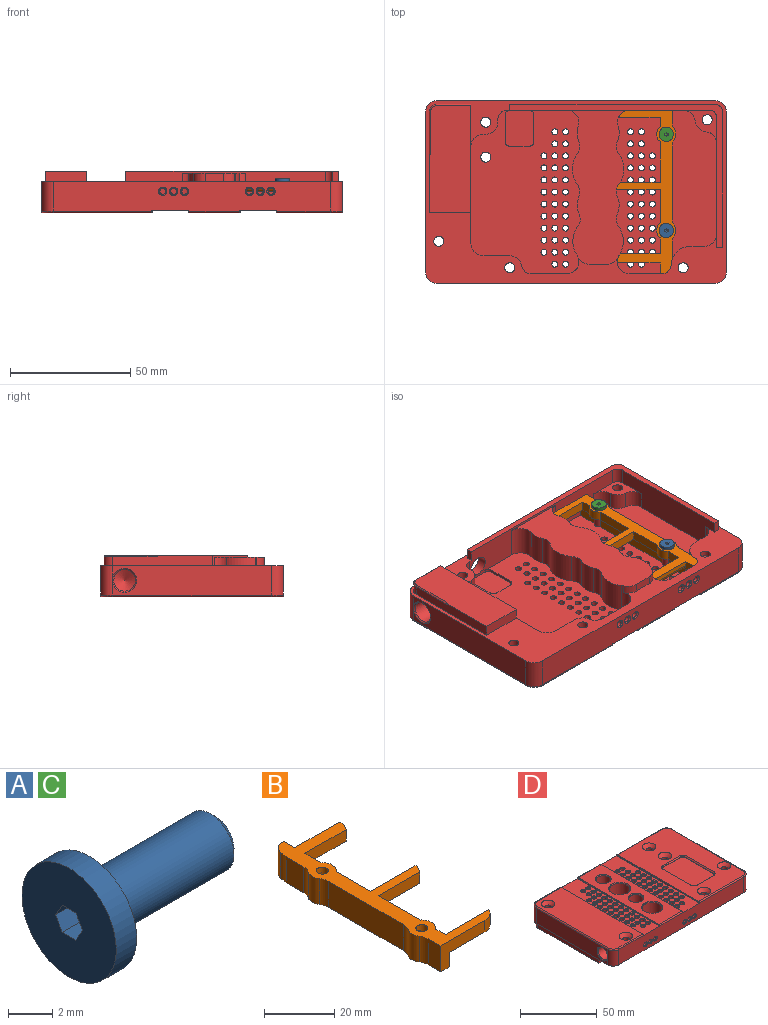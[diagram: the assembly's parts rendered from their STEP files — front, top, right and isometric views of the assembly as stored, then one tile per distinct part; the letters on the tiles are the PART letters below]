
ASSEMBLY  parts=4 mates=3
PART A: 20 faces, bbox 9.3x6x6 mm
  f0: cylinder r=3mm len=6mm, axis (-1,0,0), area 24.5mm2, adj f1,f13
  f1: plane 6x6mm, normal (-1,0,0), area 26.3mm2, adj f0,f2,f3,f4,f5,f6,f7
  f2: plane 2x0.75mm, normal (0,-0.87,0.5), area 1.7mm2, adj f1,f3,f4,f16,f17
  f3: plane 2x0.75mm, normal (0,-0.87,-0.5), area 1.7mm2, adj f1,f2,f7,f17,f18
  f4: plane 2x0.87mm, normal (0,0,1), area 1.7mm2, adj f1,f2,f5,f14,f16
  f5: plane 2x0.75mm, normal (0,0.87,0.5), area 1.7mm2, adj f1,f4,f6,f14,f15
  f6: plane 2x0.75mm, normal (0,0.87,-0.5), area 1.7mm2, adj f1,f5,f7,f15,f19
  f7: plane 2x0.87mm, normal (0,0,-1), area 1.7mm2, adj f1,f3,f6,f18,f19
  f8: cone r=0.75mm half-angle=60deg, axis (-1,0,0), area 2mm2, adj f14,f15,f16,f17,f18,f19
  f9: plane 2.39x2.39mm, normal (1,0,0), area 4.5mm2, adj f10
  f10: cone r=1.5mm half-angle=45deg, axis (-1,0,0), area 3.7mm2, adj f9,f11
  f11: cylinder r=1.5mm len=7.59mm, axis (-1,0,0), area 71.6mm2, adj f10,f12
  f12: torus R=1.6mm, axis (1,0,0), area 1.5mm2, adj f11,f13
  f13: plane 6x6mm, normal (1,0,0), area 20.2mm2, adj f0,f12
  f14: plane 0.65x0.38mm, normal (-1,0,0), area 0mm2, adj f4,f5,f8
  f15: plane 0.75x0.22mm, normal (-1,0,0), area 0mm2, adj f5,f6,f8
  f16: plane 0.65x0.38mm, normal (-1,0,0), area 0mm2, adj f2,f4,f8
  f17: plane 0.75x0.22mm, normal (-1,0,0), area 0mm2, adj f2,f3,f8
  f18: plane 0.65x0.38mm, normal (-1,0,0), area 0mm2, adj f3,f7,f8
  f19: plane 0.65x0.38mm, normal (-1,0,0), area 0mm2, adj f6,f7,f8
PART B: 47 faces, bbox 24.7x68x9 mm
  f0: plane 16.57x4mm, normal (0,-1,0), area 66.3mm2, adj f1,f21,f32,f46
  f1: plane 68x19.65mm, normal (0,0,-1), area 247.5mm2, adj f0,f3,f4,f5,f6,f9,f10,f11
  f2: plane 17.81x2mm, normal (0,1,0), area 35.6mm2, adj f3,f4,f32,f45
  f3: cylinder r=2mm len=17.84mm, axis (-1,0,0), area 55.9mm2, adj f1,f2,f4,f45
  f4: plane 6.5x4mm, normal (1,0,0), area 18.9mm2, adj f1,f2,f3,f22,f32
  f5: plane 36.42x5mm, normal (1,0,0), area 182.1mm2, adj f1,f33,f34,f36
  f6: plane 16.11x5mm, normal (1,0,0), area 80.6mm2, adj f1,f23,f33,f36
  f7: plane 4.1x3.05mm, normal (0,0,-1), area 2.8mm2, adj f29,f33,f37,f40
  f8: plane 4.1x3.05mm, normal (0,0,-1), area 2.8mm2, adj f31,f34,f38,f39
  f9: plane 17.81x9mm, normal (0,-1,0), area 88.7mm2, adj f1,f10,f30,f32,f35,f36
  f10: cylinder r=5mm len=4.58mm, axis (0,0,-1), area 23.2mm2, adj f1,f9,f11,f32
  f11: plane 17.39x4mm, normal (0,1,0), area 69.6mm2, adj f1,f10,f12,f32
  f12: plane 4x3.88mm, normal (1,0,0), area 15.5mm2, adj f1,f11,f13,f32
  f13: cylinder r=4mm len=6.25mm, axis (0,0,-1), area 28.7mm2, adj f1,f12,f14,f32
  f14: plane 16.88x4mm, normal (1,0,0), area 67.5mm2, adj f1,f13,f15,f32
  f15: plane 16.62x4mm, normal (0,-1,0), area 66.5mm2, adj f1,f14,f16,f32
  f16: cylinder r=10.7mm len=4mm, axis (0,0,-1), area 4.4mm2, adj f1,f15,f17,f32
  f17: cylinder r=5mm len=4mm, axis (0,0,-1), area 9.2mm2, adj f1,f16,f18,f32
  f18: plane 18.15x4mm, normal (0,1,0), area 72.6mm2, adj f1,f17,f19,f32
  f19: plane 13.88x4mm, normal (1,0,0), area 55.5mm2, adj f1,f18,f20,f32
  f20: cylinder r=4mm len=6.25mm, axis (0,0,-1), area 28.7mm2, adj f1,f19,f21,f32
  f21: plane 6.38x4mm, normal (1,0,0), area 25.5mm2, adj f0,f1,f20,f32
  f22: plane 4x0.63mm, normal (0,1,0), area 2.5mm2, adj f1,f4,f23,f32
  f23: cylinder r=4mm len=9mm, axis (0,0,-1), area 46.1mm2, adj f1,f6,f22,f24,f32,f36
  f24: cylinder r=8.17mm len=9mm, axis (0,0,-1), area 24mm2, adj f23,f25,f32,f36
  f25: plane 9x7.08mm, normal (-1,0,0), area 63.7mm2, adj f24,f32,f36,f42
  f26: cylinder r=4mm len=9mm, axis (0,0,-1), area 42.2mm2, adj f32,f36,f41,f42
  f27: plane 30.05x9mm, normal (-1,0,0), area 270.5mm2, adj f32,f36,f41,f43
  f28: cylinder r=4mm len=9mm, axis (0,0,-1), area 42.2mm2, adj f32,f36,f43,f44
  f29: cylinder r=1.7mm len=4mm, axis (0,0,-1), area 27.8mm2, adj f1,f7,f32,f37,f40
  f30: plane 9x5.03mm, normal (-1,0,0), area 45.2mm2, adj f9,f32,f36,f44
  f31: cylinder r=1.7mm len=4mm, axis (0,0,-1), area 27.8mm2, adj f1,f8,f32,f38,f39
  f32: plane 68x24.65mm, normal (0,0,1), area 514.5mm2, adj f0,f2,f4,f9,f10,f11,f12,f13
  f33: cylinder r=2.05mm len=7mm, axis (0,0,1), area 59.7mm2, adj f5,f6,f7,f36,f37,f40
  f34: cylinder r=2.05mm len=7mm, axis (0,0,1), area 59.7mm2, adj f5,f8,f35,f36,f38,f39
  f35: plane 8.21x5mm, normal (1,0,0), area 41.1mm2, adj f1,f9,f34,f36
  f36: plane 67.9x5mm, normal (0,0,-1), area 225.9mm2, adj f5,f6,f9,f23,f24,f25,f26,f27
  f37: plane 2x0.41mm, normal (-1,0,0), area 0.8mm2, adj f1,f7,f29,f33
  f38: plane 2x0.41mm, normal (-1,0,0), area 0.8mm2, adj f1,f8,f31,f34
  f39: plane 2x0.41mm, normal (-1,0,0), area 0.8mm2, adj f1,f8,f31,f34
  f40: plane 2x0.41mm, normal (-1,0,0), area 0.8mm2, adj f1,f7,f29,f33
  f41: cylinder r=5mm len=9mm, axis (0,0,-1), area 26.4mm2, adj f26,f27,f32,f36
  f42: cylinder r=5mm len=9mm, axis (0,0,-1), area 26.4mm2, adj f25,f26,f32,f36
  f43: cylinder r=5mm len=9mm, axis (0,0,-1), area 26.4mm2, adj f27,f28,f32,f36
  f44: cylinder r=5mm len=9mm, axis (0,0,-1), area 26.4mm2, adj f28,f30,f32,f36
  f45: cylinder r=5mm len=4mm, axis (0,0,1), area 12.8mm2, adj f1,f2,f3,f32,f46
  f46: cylinder r=10.5mm len=4mm, axis (0,0,1), area 3.5mm2, adj f0,f1,f32,f45
PART C: same geometry as A
PART D: 320 faces, bbox 126.1x77.1x17.7 mm
  f0: plane 68x45.38mm, normal (0,0,-1), area 2357.2mm2, adj f2,f4,f5,f6,f10,f12,f27,f53
  f1: plane 64x25.99mm, normal (0,0,-1), area 1135mm2, adj f2,f3,f4,f5,f6,f7,f8,f9
  f2: cylinder r=5mm len=12.4mm, axis (0,0,1), area 95.7mm2, adj f0,f1,f6,f10,f13,f221,f300
  f3: cylinder r=5mm len=12.4mm, axis (0,0,1), area 99.7mm2, adj f1,f11,f13,f25,f29,f301
  f4: cylinder r=10.7mm len=12.83mm, axis (0,0,1), area 170.6mm2, adj f0,f1,f219,f220
  f5: cylinder r=8.75mm len=12.4mm, axis (0,0,1), area 92.6mm2, adj f0,f1,f218,f219
  f6: cylinder r=10.5mm len=12.4mm, axis (0,0,1), area 158.4mm2, adj f0,f1,f2,f218
  f7: cylinder r=8.75mm len=12.4mm, axis (0,0,1), area 81.6mm2, adj f1,f29,f214,f217
  f8: cylinder r=10.7mm len=12.83mm, axis (0,0,1), area 170.6mm2, adj f1,f29,f216,f217
  f9: cylinder r=8.75mm len=12.4mm, axis (0,0,1), area 92.6mm2, adj f1,f29,f215,f216
  f10: plane 14.86x9mm, normal (0,1,0), area 123mm2, adj f0,f2,f13,f134,f221,f225,f226
  f11: cylinder r=10.5mm len=12.4mm, axis (0,0,1), area 158.4mm2, adj f1,f3,f29,f215
  f12: cylinder r=8.75mm len=12.4mm, axis (0,0,1), area 81.6mm2, adj f0,f1,f213,f220
  f13: plane 125x76mm, normal (0,0,-1), area 1906.4mm2, adj f2,f3,f10,f14,f17,f18,f25,f26
  f14: cylinder r=2.1mm len=10.7mm, axis (0,0,1), area 111mm2, adj f13,f56,f184,f185
  f15: cylinder r=5mm len=7mm, axis (0,0,1), area 51.5mm2, adj f27,f29,f52,f163
  f16: cylinder r=5mm len=7mm, axis (0,0,1), area 51.5mm2, adj f26,f29,f52,f163
  f17: plane 115x12.2mm, normal (0,-1,0), area 1339.1mm2, adj f13,f21,f22,f30,f31,f39,f137,f140
  f18: plane 115x12.2mm, normal (0,1,0), area 1344mm2, adj f13,f23,f24,f33,f34,f42,f137,f140
  f19: plane 74.4x21.1mm, normal (0,0,1), area 1094.6mm2, adj f21,f23,f150,f160,f209,f210,f211,f212
  f20: plane 74.4x26.55mm, normal (0,0,1), area 1846.1mm2, adj f22,f24,f41,f43,f44,f56,f59,f145
  f21: cylinder r=0.8mm len=21.1mm, axis (-1,0,0), area 26.5mm2, adj f17,f19,f151,f161
  f22: cylinder r=0.8mm len=22.35mm, axis (-1,0,0), area 28.1mm2, adj f17,f20,f41,f146
  f23: cylinder r=0.8mm len=21.1mm, axis (1,0,0), area 26.5mm2, adj f18,f19,f149,f159
  f24: cylinder r=0.8mm len=22.35mm, axis (1,0,0), area 28.1mm2, adj f18,f20,f44,f144
  f25: plane 13.46x9mm, normal (0,1,0), area 106.5mm2, adj f3,f13,f29,f135,f222,f223,f224
  f26: plane 54x13.42mm, normal (1,0,0), area 598.3mm2, adj f13,f16,f29,f128,f130,f163,f183,f199
  f27: plane 84x14.42mm, normal (0,-1,0), area 678.8mm2, adj f0,f1,f13,f15,f29,f128,f129,f136
  f28: plane 56x4.42mm, normal (-1,0,0), area 247.2mm2, adj f13,f60,f130,f199
  f29: plane 68x41.83mm, normal (0,0,-1), area 2259.8mm2, adj f3,f7,f8,f9,f11,f15,f16,f25
  f30: cylinder r=5mm len=12.2mm, axis (0,0,-1), area 95.8mm2, adj f13,f17,f35,f41
  f31: cylinder r=5mm len=12.2mm, axis (0,0,-1), area 95.8mm2, adj f13,f17,f32,f37
  f32: plane 66x12.2mm, normal (1,0,0), area 726.7mm2, adj f13,f31,f33,f38,f197
  f33: cylinder r=5mm len=12.2mm, axis (0,0,-1), area 95.8mm2, adj f13,f18,f32,f40
  f34: cylinder r=5mm len=12.2mm, axis (0,0,-1), area 95.8mm2, adj f13,f18,f35,f44
  f35: plane 66x12.2mm, normal (-1,0,0), area 726.7mm2, adj f13,f30,f34,f43,f198
  f36: plane 74.4x44.95mm, normal (0,0,1), area 2425.2mm2, adj f37,f38,f39,f40,f42,f57,f58,f132
  f37: torus R=4.2mm, axis (0,0,1), area 9.3mm2, adj f31,f36,f38,f39
  f38: cylinder r=0.8mm len=66mm, axis (0,-1,0), area 82.9mm2, adj f32,f36,f37,f40
  f39: cylinder r=0.8mm len=40.75mm, axis (-1,0,0), area 51.2mm2, adj f17,f36,f37,f156
  f40: torus R=4.2mm, axis (0,0,1), area 9.3mm2, adj f33,f36,f38,f42
  f41: torus R=4.2mm, axis (0,0,1), area 9.3mm2, adj f20,f22,f30,f43
  f42: cylinder r=0.8mm len=40.75mm, axis (1,0,0), area 51.2mm2, adj f18,f36,f40,f154
  f43: cylinder r=0.8mm len=66mm, axis (0,1,0), area 82.9mm2, adj f20,f35,f41,f44
  f44: torus R=4.2mm, axis (0,0,1), area 9.3mm2, adj f20,f24,f34,f43
  f45: cylinder r=6.7mm len=13.4mm, axis (0,0,1), area 517.8mm2, adj f207,f210
  f46: cylinder r=4.75mm len=12.3mm, axis (0,0,1), area 367.1mm2, adj f206,f211
  f47: cylinder r=6.5mm len=13mm, axis (0,0,1), area 502.3mm2, adj f208,f212
  f48: cylinder r=4.75mm len=12.3mm, axis (0,0,1), area 367.1mm2, adj f205,f209
  f49: cylinder r=2.1mm len=10.7mm, axis (0,0,1), area 141.2mm2, adj f13,f58
  f50: cylinder r=2.1mm len=10.7mm, axis (0,0,1), area 141.2mm2, adj f13,f57
  f51: cylinder r=2.1mm len=8.7mm, axis (0,0,1), area 114.8mm2, adj f59,f163
  f52: cylinder r=5mm len=7mm, axis (0,0,1), area 48mm2, adj f15,f16,f29,f163
  f53: cylinder r=5mm len=9mm, axis (0,0,1), area 63.2mm2, adj f0,f13,f133,f134
  f54: cylinder r=5mm len=9mm, axis (0,0,1), area 70.7mm2, adj f0,f13,f55,f200
  f55: plane 9x1mm, normal (-1,0,0), area 9mm2, adj f0,f13,f54,f136
  f56: cone r=2.1mm half-angle=45deg, axis (0,0,1), area 66.4mm2, adj f14,f20
  f57: cone r=2.1mm half-angle=45deg, axis (0,0,1), area 66.4mm2, adj f36,f50
  f58: cone r=2.1mm half-angle=45deg, axis (0,0,1), area 66.4mm2, adj f36,f49
  f59: cone r=2.1mm half-angle=45deg, axis (0,0,1), area 66.4mm2, adj f20,f51
  f60: cylinder r=3.5mm len=4.42mm, axis (0,0,1), area 24.3mm2, adj f13,f28,f61,f199
  f61: plane 85x4.42mm, normal (0,1,0), area 375.3mm2, adj f13,f60,f129,f199
  f62: cylinder r=1.25mm len=2.5mm, axis (0,0,1), area 19.6mm2, adj f29,f290
  f63: cylinder r=1.25mm len=2.5mm, axis (0,0,1), area 19.6mm2, adj f29,f230
  f64: cylinder r=1.25mm len=2.5mm, axis (0,0,1), area 19.6mm2, adj f0,f259
  f65: cylinder r=1.25mm len=2.5mm, axis (0,0,1), area 19.6mm2, adj f0,f260
  f66: cylinder r=1.25mm len=2.5mm, axis (0,0,1), area 19.6mm2, adj f0,f264
  f67: cylinder r=1.25mm len=2.5mm, axis (0,0,1), area 19.6mm2, adj f0,f265
  f68: cylinder r=1.25mm len=2.5mm, axis (0,0,1), area 19.6mm2, adj f0,f279
  f69: cylinder r=1.25mm len=2.5mm, axis (0,0,1), area 19.6mm2, adj f0,f284
  f70: cylinder r=1.25mm len=2.5mm, axis (0,0,1), area 19.6mm2, adj f0,f281
  f71: cylinder r=1.25mm len=2.5mm, axis (0,0,1), area 19.6mm2, adj f0,f268
  f72: cylinder r=1.25mm len=2.5mm, axis (0,0,1), area 19.6mm2, adj f29,f273
  f73: cylinder r=1.25mm len=2.5mm, axis (0,0,1), area 19.6mm2, adj f29,f277
  f74: cylinder r=1.25mm len=2.5mm, axis (0,0,1), area 19.6mm2, adj f29,f288
  f75: cylinder r=1.25mm len=2.5mm, axis (0,0,1), area 19.6mm2, adj f29,f289
  f76: cylinder r=1.25mm len=2.5mm, axis (0,0,1), area 19.6mm2, adj f29,f276
  f77: cylinder r=1.25mm len=2.5mm, axis (0,0,1), area 19.6mm2, adj f29,f278
  f78: cylinder r=1.25mm len=2.5mm, axis (0,0,1), area 19.6mm2, adj f29,f274
  f79: cylinder r=1.25mm len=2.5mm, axis (0,0,1), area 19.6mm2, adj f29,f275
  f80: cylinder r=1.25mm len=2.5mm, axis (0,0,1), area 19.6mm2, adj f29,f291
  f81: cylinder r=1.25mm len=2.5mm, axis (0,0,1), area 19.6mm2, adj f0,f292
  f82: cylinder r=1.25mm len=2.5mm, axis (0,0,1), area 19.6mm2, adj f0,f294
  f83: cylinder r=1.25mm len=2.5mm, axis (0,0,1), area 19.6mm2, adj f0,f293
  f84: cylinder r=1.25mm len=2.5mm, axis (0,0,1), area 19.6mm2, adj f0,f286
  f85: cylinder r=1.25mm len=2.5mm, axis (0,0,1), area 19.6mm2, adj f0,f285
  f86: cylinder r=1.25mm len=2.5mm, axis (0,0,1), area 19.6mm2, adj f0,f280
  f87: cylinder r=1.25mm len=2.5mm, axis (0,0,1), area 19.6mm2, adj f29,f256
  f88: cylinder r=1.25mm len=2.5mm, axis (0,0,1), area 19.6mm2, adj f29,f250
  f89: cylinder r=1.25mm len=2.5mm, axis (0,0,1), area 19.6mm2, adj f29,f251
  f90: cylinder r=1.25mm len=2.5mm, axis (0,0,1), area 19.6mm2, adj f29,f254
  f91: cylinder r=1.25mm len=2.5mm, axis (0,0,1), area 19.6mm2, adj f29,f253
  f92: cylinder r=1.25mm len=2.5mm, axis (0,0,1), area 19.6mm2, adj f29,f269
  f93: cylinder r=1.25mm len=2.5mm, axis (0,0,1), area 19.6mm2, adj f29,f270
  f94: cylinder r=1.25mm len=2.5mm, axis (0,0,1), area 19.6mm2, adj f29,f271
  f95: cylinder r=1.25mm len=2.5mm, axis (0,0,1), area 19.6mm2, adj f29,f272
  f96: cylinder r=1.25mm len=2.5mm, axis (0,0,1), area 19.6mm2, adj f0,f234
  f97: cylinder r=1.25mm len=2.5mm, axis (0,0,1), area 19.6mm2, adj f0,f233
  f98: cylinder r=1.25mm len=2.5mm, axis (0,0,1), area 19.6mm2, adj f29,f243
  f99: cylinder r=1.25mm len=2.5mm, axis (0,0,1), area 19.6mm2, adj f29,f242
  f100: cylinder r=1.25mm len=2.5mm, axis (0,0,1), area 19.6mm2, adj f29,f239
  f101: cylinder r=1.25mm len=2.5mm, axis (0,0,1), area 19.6mm2, adj f0,f232
  f102: cylinder r=1.25mm len=2.5mm, axis (0,0,1), area 19.6mm2, adj f0,f231
  f103: cylinder r=1.25mm len=2.5mm, axis (0,0,1), area 19.6mm2, adj f0,f237
  f104: cylinder r=1.25mm len=2.5mm, axis (0,0,1), area 19.6mm2, adj f29,f249
  f105: cylinder r=1.25mm len=2.5mm, axis (0,0,1), area 19.6mm2, adj f29,f241
  f106: cylinder r=1.25mm len=2.5mm, axis (0,0,1), area 19.6mm2, adj f29,f240
  f107: cylinder r=1.25mm len=2.5mm, axis (0,0,1), area 19.6mm2, adj f0,f236
  f108: cylinder r=1.25mm len=2.5mm, axis (0,0,1), area 19.6mm2, adj f29,f244
  f109: cylinder r=1.25mm len=2.5mm, axis (0,0,1), area 19.6mm2, adj f29,f248
  f110: cylinder r=1.25mm len=2.5mm, axis (0,0,1), area 19.6mm2, adj f29,f247
  f111: cylinder r=1.25mm len=2.5mm, axis (0,0,1), area 19.6mm2, adj f0,f246
  f112: cylinder r=1.25mm len=2.5mm, axis (0,0,1), area 19.6mm2, adj f0,f263
  f113: cylinder r=1.25mm len=2.5mm, axis (0,0,1), area 19.6mm2, adj f0,f266
  f114: cylinder r=1.25mm len=2.5mm, axis (0,0,1), area 19.6mm2, adj f0,f267
  f115: cylinder r=1.25mm len=2.5mm, axis (0,0,1), area 19.6mm2, adj f0,f282
  f116: cylinder r=1.25mm len=2.5mm, axis (0,0,1), area 19.6mm2, adj f29,f257
  f117: cylinder r=1.25mm len=2.5mm, axis (0,0,1), area 19.6mm2, adj f0,f258
  f118: cylinder r=1.25mm len=2.5mm, axis (0,0,1), area 19.6mm2, adj f0,f235
  f119: cylinder r=1.25mm len=2.5mm, axis (0,0,1), area 19.6mm2, adj f29,f255
  f120: cylinder r=1.25mm len=2.5mm, axis (0,0,1), area 19.6mm2, adj f0,f229
  f121: cylinder r=1.25mm len=2.5mm, axis (0,0,1), area 19.6mm2, adj f0,f238
  f122: cylinder r=1.25mm len=2.5mm, axis (0,0,1), area 19.6mm2, adj f0,f245
  f123: cylinder r=1.25mm len=2.5mm, axis (0,0,1), area 19.6mm2, adj f0,f283
  f124: cylinder r=1.25mm len=2.5mm, axis (0,0,1), area 19.6mm2, adj f29,f287
  f125: cylinder r=1.25mm len=2.5mm, axis (0,0,1), area 19.6mm2, adj f29,f252
  f126: cylinder r=1.25mm len=2.5mm, axis (0,0,1), area 19.6mm2, adj f0,f262
  f127: cylinder r=1.25mm len=2.5mm, axis (0,0,1), area 19.6mm2, adj f0,f261
  f128: cylinder r=3mm len=6.42mm, axis (0,0,-1), area 30.2mm2, adj f26,f27,f163,f199
  f129: plane 4.42x2.5mm, normal (1,0,0), area 11mm2, adj f13,f27,f61,f199
  f130: plane 4.42x2.5mm, normal (0,-1,0), area 11mm2, adj f13,f26,f28,f199
  f131: cylinder r=2.1mm len=10.7mm, axis (0,0,1), area 141.2mm2, adj f13,f132
  f132: cone r=2.1mm half-angle=45deg, axis (0,0,1), area 66.4mm2, adj f36,f131
  f133: plane 11.15x9mm, normal (0,1,0), area 100.3mm2, adj f0,f13,f53,f202
  f134: cylinder r=4mm len=9mm, axis (0,0,1), area 50.5mm2, adj f0,f10,f13,f53
  f135: cylinder r=4mm len=9mm, axis (0,0,1), area 50.5mm2, adj f13,f25,f29,f182
  f136: cylinder r=4mm len=9mm, axis (0,0,-1), area 56.5mm2, adj f0,f13,f27,f55
  f137: plane 76x15.4mm, normal (0,0,1), area 822.6mm2, adj f17,f18,f138,f139,f143,f147,f148,f152
  f138: plane 75.6x0.8mm, normal (-1,0,0), area 60.3mm2, adj f137,f148,f149,f150,f151,f152
  f139: plane 75.6x0.8mm, normal (1,0,0), area 60.3mm2, adj f137,f143,f144,f145,f146,f147
  f140: plane 76x15.4mm, normal (0,0,1), area 822.6mm2, adj f17,f18,f141,f142,f153,f157,f158,f162
  f141: plane 75.6x0.8mm, normal (1,0,0), area 60.3mm2, adj f140,f158,f159,f160,f161,f162
  f142: plane 75.6x0.8mm, normal (-1,0,0), area 60.3mm2, adj f140,f153,f154,f155,f156,f157
  f143: plane 0.2x0.2mm, normal (0.71,0.71,0), area 0.1mm2, adj f18,f137,f139,f144
  f144: cone r=0.8mm half-angle=45deg, axis (-1,0,0), area 0.3mm2, adj f24,f139,f143,f145
  f145: plane 74.4x0.2mm, normal (0.71,0,0.71), area 21mm2, adj f20,f139,f144,f146
  f146: cone r=0.8mm half-angle=45deg, axis (-1,0,0), area 0.3mm2, adj f22,f139,f145,f147
  f147: plane 0.2x0.2mm, normal (0.71,-0.71,0), area 0.1mm2, adj f17,f137,f139,f146
  f148: plane 0.2x0.2mm, normal (-0.71,0.71,0), area 0.1mm2, adj f18,f137,f138,f149
  f149: cone r=0.6mm half-angle=45deg, axis (1,0,0), area 0.3mm2, adj f23,f138,f148,f150
  f150: plane 74.4x0.2mm, normal (-0.71,0,0.71), area 21mm2, adj f19,f138,f149,f151
  f151: cone r=0.6mm half-angle=45deg, axis (1,0,0), area 0.3mm2, adj f21,f138,f150,f152
  f152: plane 0.2x0.2mm, normal (-0.71,-0.71,0), area 0.1mm2, adj f17,f137,f138,f151
  f153: plane 0.2x0.2mm, normal (-0.71,0.71,0), area 0.1mm2, adj f18,f140,f142,f154
  f154: cone r=0.6mm half-angle=45deg, axis (1,0,0), area 0.3mm2, adj f42,f142,f153,f155
  f155: plane 74.4x0.2mm, normal (-0.71,0,0.71), area 21mm2, adj f36,f142,f154,f156
  f156: cone r=0.6mm half-angle=45deg, axis (1,0,0), area 0.3mm2, adj f39,f142,f155,f157
  f157: plane 0.2x0.2mm, normal (-0.71,-0.71,0), area 0.1mm2, adj f17,f140,f142,f156
  f158: plane 0.2x0.2mm, normal (0.71,0.71,0), area 0.1mm2, adj f18,f140,f141,f159
  f159: cone r=0.8mm half-angle=45deg, axis (-1,0,0), area 0.3mm2, adj f23,f141,f158,f160
  f160: plane 74.4x0.2mm, normal (0.71,0,0.71), area 21mm2, adj f19,f141,f159,f161
  f161: cone r=0.8mm half-angle=45deg, axis (-1,0,0), area 0.3mm2, adj f21,f141,f160,f162
  f162: plane 0.2x0.2mm, normal (0.71,-0.71,0), area 0.1mm2, adj f17,f140,f141,f161
  f163: plane 13.95x13.95mm, normal (0,0,-1), area 70.1mm2, adj f15,f16,f26,f27,f51,f52,f128
  f164: cylinder r=2.5mm len=2.5mm, axis (0,0,1), area 1mm2, adj f165,f171,f172,f175
  f165: plane 15x0.25mm, normal (0,1,0), area 3.8mm2, adj f164,f166,f172,f177
  f166: cylinder r=2.5mm len=2.5mm, axis (0,0,1), area 1mm2, adj f165,f167,f172,f179
  f167: plane 25x0.25mm, normal (-1,0,0), area 6.3mm2, adj f166,f168,f172,f180
  f168: cylinder r=2.5mm len=2.5mm, axis (0,0,1), area 1mm2, adj f167,f169,f172,f178
  f169: plane 15x0.25mm, normal (0,-1,0), area 3.8mm2, adj f168,f170,f172,f176
  f170: cylinder r=2.5mm len=2.5mm, axis (0,0,1), area 1mm2, adj f169,f171,f172,f174
  f171: plane 25x0.25mm, normal (1,0,0), area 6.3mm2, adj f164,f170,f172,f173
  f172: plane 30x20mm, normal (0,0,1), area 594.6mm2, adj f164,f165,f166,f167,f168,f169,f170,f171
  f173: plane 25x0.75mm, normal (0.71,0,0.71), area 26.5mm2, adj f36,f171,f174,f175
  f174: cone r=2.5mm half-angle=45deg, axis (0,0,1), area 4.8mm2, adj f36,f170,f173,f176
  f175: cone r=2.5mm half-angle=45deg, axis (0,0,1), area 4.8mm2, adj f36,f164,f173,f177
  f176: plane 15x0.75mm, normal (0,-0.71,0.71), area 15.9mm2, adj f36,f169,f174,f178
  f177: plane 15x0.75mm, normal (0,0.71,0.71), area 15.9mm2, adj f36,f165,f175,f179
  f178: cone r=2.5mm half-angle=45deg, axis (0,0,1), area 4.8mm2, adj f36,f168,f176,f180
  f179: cone r=2.5mm half-angle=45deg, axis (0,0,1), area 4.8mm2, adj f36,f166,f177,f180
  f180: plane 25x0.75mm, normal (-0.71,0,0.71), area 26.5mm2, adj f36,f167,f178,f179
  f181: plane 9x5.76mm, normal (0,1,0), area 51.9mm2, adj f13,f29,f182,f183
  f182: cylinder r=8.17mm len=9mm, axis (0,0,1), area 115.5mm2, adj f13,f29,f135,f181
  f183: cylinder r=5mm len=9mm, axis (0,0,1), area 70.7mm2, adj f13,f26,f29,f181
  f184: cone r=0mm half-angle=59deg, axis (-1,0,0), area 52.3mm2, adj f14,f185
  f185: cylinder r=4.5mm len=16.5mm, axis (-1,0,0), area 456.8mm2, adj f14,f184,f198
  f186: cone r=0mm half-angle=59deg, axis (1,0,0), area 74.2mm2, adj f187
  f187: cylinder r=4.5mm len=16.5mm, axis (1,0,0), area 466.5mm2, adj f186,f197
  f188: cylinder r=3.5mm len=3.92mm, axis (0,0,1), area 21.5mm2, adj f13,f189,f192,f195
  f189: plane 41.5x4.42mm, normal (1,0,0), area 174mm2, adj f13,f188,f190,f193,f194,f311
  f190: plane 17.35x4.42mm, normal (0,-1,0), area 76.6mm2, adj f13,f189,f191,f193
  f191: plane 58x13.42mm, normal (-1,0,0), area 563mm2, adj f0,f13,f190,f192,f193,f196,f201,f202
  f192: plane 13.85x3.92mm, normal (0,1,0), area 54.2mm2, adj f13,f188,f191,f196
  f193: plane 44.5x17.35mm, normal (0,0,-1), area 759.9mm2, adj f189,f190,f191,f194,f195,f196,f311
  f194: plane 18.74x0.74mm, normal (0.71,0,-0.71), area 12.4mm2, adj f189,f193,f195,f311
  f195: cone r=3mm half-angle=45deg, axis (0,0,1), area 3.6mm2, adj f188,f193,f194,f196
  f196: plane 13.85x0.5mm, normal (0,0.71,-0.71), area 9.8mm2, adj f191,f192,f193,f195
  f197: cone r=4.5mm half-angle=45deg, axis (1,0,0), area 21.1mm2, adj f32,f187
  f198: cone r=4.5mm half-angle=45deg, axis (-1,0,0), area 21.1mm2, adj f35,f185
  f199: plane 88.5x59.5mm, normal (0,0,-1), area 363.1mm2, adj f26,f27,f28,f60,f61,f128,f129,f130
  f200: plane 9x1.15mm, normal (0,-1,0), area 10.3mm2, adj f0,f13,f54,f201
  f201: cylinder r=5mm len=9mm, axis (0,0,-1), area 70.7mm2, adj f0,f13,f191,f200
  f202: cylinder r=5mm len=9mm, axis (0,0,-1), area 70.7mm2, adj f0,f13,f133,f191
  f203: cylinder r=2.1mm len=4.2mm, axis (0,0,1), area 22.4mm2, adj f0,f204
  f204: cone r=2.1mm half-angle=45deg, axis (0,0,1), area 66.4mm2, adj f36,f203
  f205: plane 9.5x9.5mm, normal (0,0,1), area 70.9mm2, adj f48
  f206: plane 9.5x9.5mm, normal (0,0,1), area 70.9mm2, adj f46
  f207: plane 13.4x13.4mm, normal (0,0,1), area 141mm2, adj f45
  f208: plane 13x13mm, normal (0,0,1), area 132.7mm2, adj f47
  f209: cone r=4.75mm half-angle=30deg, axis (0,0,1), area 25.1mm2, adj f19,f48
  f210: cone r=6.7mm half-angle=30deg, axis (0,0,1), area 35.1mm2, adj f19,f45
  f211: cone r=4.75mm half-angle=30deg, axis (0,0,1), area 25.1mm2, adj f19,f46
  f212: cone r=6.5mm half-angle=30deg, axis (0,0,1), area 34mm2, adj f19,f47
  f213: cylinder r=5mm len=12.4mm, axis (0,0,1), area 118.1mm2, adj f0,f1,f12,f27
  f214: cylinder r=5mm len=12.4mm, axis (0,0,1), area 118.1mm2, adj f1,f7,f27,f29
  f215: cylinder r=5mm len=12.4mm, axis (0,0,1), area 66.4mm2, adj f1,f9,f11,f29
  f216: cylinder r=5mm len=12.4mm, axis (0,0,1), area 65.8mm2, adj f1,f8,f9,f29
  f217: cylinder r=5mm len=12.4mm, axis (0,0,1), area 65.8mm2, adj f1,f7,f8,f29
  f218: cylinder r=5mm len=12.4mm, axis (0,0,1), area 66.4mm2, adj f0,f1,f5,f6
  f219: cylinder r=5mm len=12.4mm, axis (0,0,1), area 65.8mm2, adj f0,f1,f4,f5
  f220: cylinder r=5mm len=12.4mm, axis (0,0,1), area 65.8mm2, adj f0,f1,f4,f12
  f221: cylinder r=1.25mm len=3.86mm, axis (0,-1,0), area 28.4mm2, adj f2,f10,f295
  f222: cylinder r=1.25mm len=3.5mm, axis (0,-1,0), area 27.5mm2, adj f25,f296
  f223: cylinder r=1.25mm len=3.5mm, axis (0,-1,0), area 27.5mm2, adj f25,f297
  f224: cylinder r=1.25mm len=3.5mm, axis (0,-1,0), area 27.5mm2, adj f25,f298
  f225: cylinder r=1.25mm len=3.5mm, axis (0,-1,0), area 27.5mm2, adj f10,f227
  f226: cylinder r=1.25mm len=3.5mm, axis (0,-1,0), area 27.5mm2, adj f10,f228
  f227: cone r=1.25mm half-angle=45deg, axis (0,-1,0), area 6.7mm2, adj f17,f225
  f228: cone r=1.25mm half-angle=45deg, axis (0,-1,0), area 6.7mm2, adj f17,f226
  f229: cone r=1.25mm half-angle=45deg, axis (0,0,1), area 6.7mm2, adj f120,f140
  f230: cone r=1.25mm half-angle=45deg, axis (0,0,1), area 6.7mm2, adj f63,f137
  f231: cone r=1.25mm half-angle=45deg, axis (0,0,1), area 6.7mm2, adj f102,f140
  f232: cone r=1.25mm half-angle=45deg, axis (0,0,1), area 6.7mm2, adj f101,f140
  f233: cone r=1.25mm half-angle=45deg, axis (0,0,1), area 6.7mm2, adj f97,f140
  f234: cone r=1.25mm half-angle=45deg, axis (0,0,1), area 6.7mm2, adj f96,f140
  f235: cone r=1.25mm half-angle=45deg, axis (0,0,1), area 6.7mm2, adj f118,f140
  f236: cone r=1.25mm half-angle=45deg, axis (0,0,1), area 6.7mm2, adj f107,f140
  f237: cone r=1.25mm half-angle=45deg, axis (0,0,1), area 6.7mm2, adj f103,f140
  f238: cone r=1.25mm half-angle=45deg, axis (0,0,1), area 6.7mm2, adj f121,f140
  f239: cone r=1.25mm half-angle=45deg, axis (0,0,1), area 6.7mm2, adj f100,f137
  f240: cone r=1.25mm half-angle=45deg, axis (0,0,1), area 6.7mm2, adj f106,f137
  f241: cone r=1.25mm half-angle=45deg, axis (0,0,1), area 6.7mm2, adj f105,f137
  f242: cone r=1.25mm half-angle=45deg, axis (0,0,1), area 6.7mm2, adj f99,f137
  f243: cone r=1.25mm half-angle=45deg, axis (0,0,1), area 6.7mm2, adj f98,f137
  f244: cone r=1.25mm half-angle=45deg, axis (0,0,1), area 6.7mm2, adj f108,f137
  f245: cone r=1.25mm half-angle=45deg, axis (0,0,1), area 6.7mm2, adj f122,f140
  f246: cone r=1.25mm half-angle=45deg, axis (0,0,1), area 6.7mm2, adj f111,f140
  f247: cone r=1.25mm half-angle=45deg, axis (0,0,1), area 6.7mm2, adj f110,f137
  f248: cone r=1.25mm half-angle=45deg, axis (0,0,1), area 6.7mm2, adj f109,f137
  f249: cone r=1.25mm half-angle=45deg, axis (0,0,1), area 6.7mm2, adj f104,f137
  f250: cone r=1.25mm half-angle=45deg, axis (0,0,1), area 6.7mm2, adj f88,f137
  f251: cone r=1.25mm half-angle=45deg, axis (0,0,1), area 6.7mm2, adj f89,f137
  f252: cone r=1.25mm half-angle=45deg, axis (0,0,1), area 6.7mm2, adj f125,f137
  f253: cone r=1.25mm half-angle=45deg, axis (0,0,1), area 6.7mm2, adj f91,f137
  f254: cone r=1.25mm half-angle=45deg, axis (0,0,1), area 6.7mm2, adj f90,f137
  f255: cone r=1.25mm half-angle=45deg, axis (0,0,1), area 6.7mm2, adj f119,f137
  f256: cone r=1.25mm half-angle=45deg, axis (0,0,1), area 6.7mm2, adj f87,f137
  f257: cone r=1.25mm half-angle=45deg, axis (0,0,1), area 6.7mm2, adj f116,f137
  f258: cone r=1.25mm half-angle=45deg, axis (0,0,1), area 6.7mm2, adj f117,f140
  f259: cone r=1.25mm half-angle=45deg, axis (0,0,1), area 6.7mm2, adj f64,f140
  f260: cone r=1.25mm half-angle=45deg, axis (0,0,1), area 6.7mm2, adj f65,f140
  f261: cone r=1.25mm half-angle=45deg, axis (0,0,1), area 6.7mm2, adj f127,f140
  f262: cone r=1.25mm half-angle=45deg, axis (0,0,1), area 6.7mm2, adj f126,f140
  f263: cone r=1.25mm half-angle=45deg, axis (0,0,1), area 6.7mm2, adj f112,f140
  f264: cone r=1.25mm half-angle=45deg, axis (0,0,1), area 6.7mm2, adj f66,f140
  f265: cone r=1.25mm half-angle=45deg, axis (0,0,1), area 6.7mm2, adj f67,f140
  f266: cone r=1.25mm half-angle=45deg, axis (0,0,1), area 6.7mm2, adj f113,f140
  f267: cone r=1.25mm half-angle=45deg, axis (0,0,1), area 6.7mm2, adj f114,f140
  f268: cone r=1.25mm half-angle=45deg, axis (0,0,1), area 6.7mm2, adj f71,f140
  f269: cone r=1.25mm half-angle=45deg, axis (0,0,1), area 6.7mm2, adj f92,f137
  f270: cone r=1.25mm half-angle=45deg, axis (0,0,1), area 6.7mm2, adj f93,f137
  f271: cone r=1.25mm half-angle=45deg, axis (0,0,1), area 6.7mm2, adj f94,f137
  f272: cone r=1.25mm half-angle=45deg, axis (0,0,1), area 6.7mm2, adj f95,f137
  f273: cone r=1.25mm half-angle=45deg, axis (0,0,1), area 6.7mm2, adj f72,f137
  f274: cone r=1.25mm half-angle=45deg, axis (0,0,1), area 6.7mm2, adj f78,f137
  f275: cone r=1.25mm half-angle=45deg, axis (0,0,1), area 6.7mm2, adj f79,f137
  f276: cone r=1.25mm half-angle=45deg, axis (0,0,1), area 6.7mm2, adj f76,f137
  f277: cone r=1.25mm half-angle=45deg, axis (0,0,1), area 6.7mm2, adj f73,f137
  f278: cone r=1.25mm half-angle=45deg, axis (0,0,1), area 6.7mm2, adj f77,f137
  f279: cone r=1.25mm half-angle=45deg, axis (0,0,1), area 6.7mm2, adj f68,f140
  f280: cone r=1.25mm half-angle=45deg, axis (0,0,1), area 6.7mm2, adj f86,f140
  f281: cone r=1.25mm half-angle=45deg, axis (0,0,1), area 6.7mm2, adj f70,f140
  f282: cone r=1.25mm half-angle=45deg, axis (0,0,1), area 6.7mm2, adj f115,f140
  f283: cone r=1.25mm half-angle=45deg, axis (0,0,1), area 6.7mm2, adj f123,f140
  f284: cone r=1.25mm half-angle=45deg, axis (0,0,1), area 6.7mm2, adj f69,f140
  f285: cone r=1.25mm half-angle=45deg, axis (0,0,1), area 6.7mm2, adj f85,f140
  f286: cone r=1.25mm half-angle=45deg, axis (0,0,1), area 6.7mm2, adj f84,f140
  f287: cone r=1.25mm half-angle=45deg, axis (0,0,1), area 6.7mm2, adj f124,f137
  f288: cone r=1.25mm half-angle=45deg, axis (0,0,1), area 6.7mm2, adj f74,f137
  f289: cone r=1.25mm half-angle=45deg, axis (0,0,1), area 6.7mm2, adj f75,f137
  f290: cone r=1.25mm half-angle=45deg, axis (0,0,1), area 6.7mm2, adj f62,f137
  f291: cone r=1.25mm half-angle=45deg, axis (0,0,1), area 6.7mm2, adj f80,f137
  f292: cone r=1.25mm half-angle=45deg, axis (0,0,1), area 6.7mm2, adj f81,f140
  f293: cone r=1.25mm half-angle=45deg, axis (0,0,1), area 6.7mm2, adj f83,f140
  f294: cone r=1.25mm half-angle=45deg, axis (0,0,1), area 6.7mm2, adj f82,f140
  f295: cone r=1.25mm half-angle=45deg, axis (0,-1,0), area 6.7mm2, adj f17,f221
  f296: cone r=1.25mm half-angle=45deg, axis (0,-1,0), area 6.7mm2, adj f17,f222
  f297: cone r=1.25mm half-angle=45deg, axis (0,-1,0), area 6.7mm2, adj f17,f223
  f298: cone r=1.25mm half-angle=45deg, axis (0,-1,0), area 6.7mm2, adj f17,f224
  f299: plane 7.59x3.4mm, normal (0,-1,0), area 25.8mm2, adj f1,f13,f300,f301
  f300: cylinder r=5mm len=4.58mm, axis (0,0,1), area 19.7mm2, adj f1,f2,f13,f299
  f301: cylinder r=5mm len=4.58mm, axis (0,0,1), area 19.7mm2, adj f1,f3,f13,f299
  f302: cylinder r=4.1mm len=8.2mm, axis (0,-1,0), area 103mm2, adj f18,f27
  f303: cylinder r=2mm len=2mm, axis (0,0,-1), area 3.1mm2, adj f0,f27,f304,f310
  f304: plane 11x1mm, normal (-1,0,0), area 11mm2, adj f0,f303,f305,f310
  f305: cylinder r=2mm len=2mm, axis (0,0,-1), area 3.1mm2, adj f0,f304,f306,f310
  f306: plane 8x1mm, normal (0,1,0), area 8mm2, adj f0,f305,f307,f310
  f307: cylinder r=2mm len=2mm, axis (0,0,-1), area 3.1mm2, adj f0,f306,f308,f310
  f308: plane 11x1mm, normal (1,0,0), area 11mm2, adj f0,f307,f309,f310
  f309: cylinder r=2mm len=2mm, axis (0,0,-1), area 3.1mm2, adj f0,f27,f308,f310
  f310: plane 15x12mm, normal (0,0,-1), area 176.6mm2, adj f27,f303,f304,f305,f306,f307,f308,f309
  f311: cylinder r=2mm len=1.32mm, axis (0,0,-1), area 0.4mm2, adj f189,f193,f194
  f312: cylinder r=2mm len=7mm, axis (0,0,1), area 88mm2, adj f29,f313
  f313: plane 4x4mm, normal (0,0,-1), area 7.7mm2, adj f312,f319
  f314: cylinder r=2mm len=7mm, axis (0,0,1), area 88mm2, adj f29,f315
  f315: plane 4x4mm, normal (0,0,-1), area 7.7mm2, adj f314,f317
  f316: cone r=0mm half-angle=59deg, axis (0,0,-1), area 5.7mm2, adj f317
  f317: cylinder r=1.25mm len=6mm, axis (0,0,-1), area 47.1mm2, adj f315,f316
  f318: cone r=0mm half-angle=59deg, axis (0,0,-1), area 5.7mm2, adj f319
  f319: cylinder r=1.25mm len=6mm, axis (0,0,-1), area 47.1mm2, adj f313,f318
PLACE A rot(axis=(0.71,0,-0.71),180deg) t=(99.2,17,13)mm
PLACE B rot(axis=(0,0,1),180deg) t=(96.7,34,11)mm
PLACE C rot(axis=(0.71,0,-0.71),180deg) t=(99.2,57,13)mm
PLACE D rot(axis=(0,1,0),180deg) t=(70.2,33,13)mm
MATE fastened D.f312 <-> B.f20  axis (0,0,1) through (99.2,17,11)mm
MATE fastened B.f20 <-> A.f0  axis (0,0,1) through (99.2,17,13)mm
MATE fastened B.f13 <-> C.f0  axis (0,0,1) through (99.2,57,13)mm
